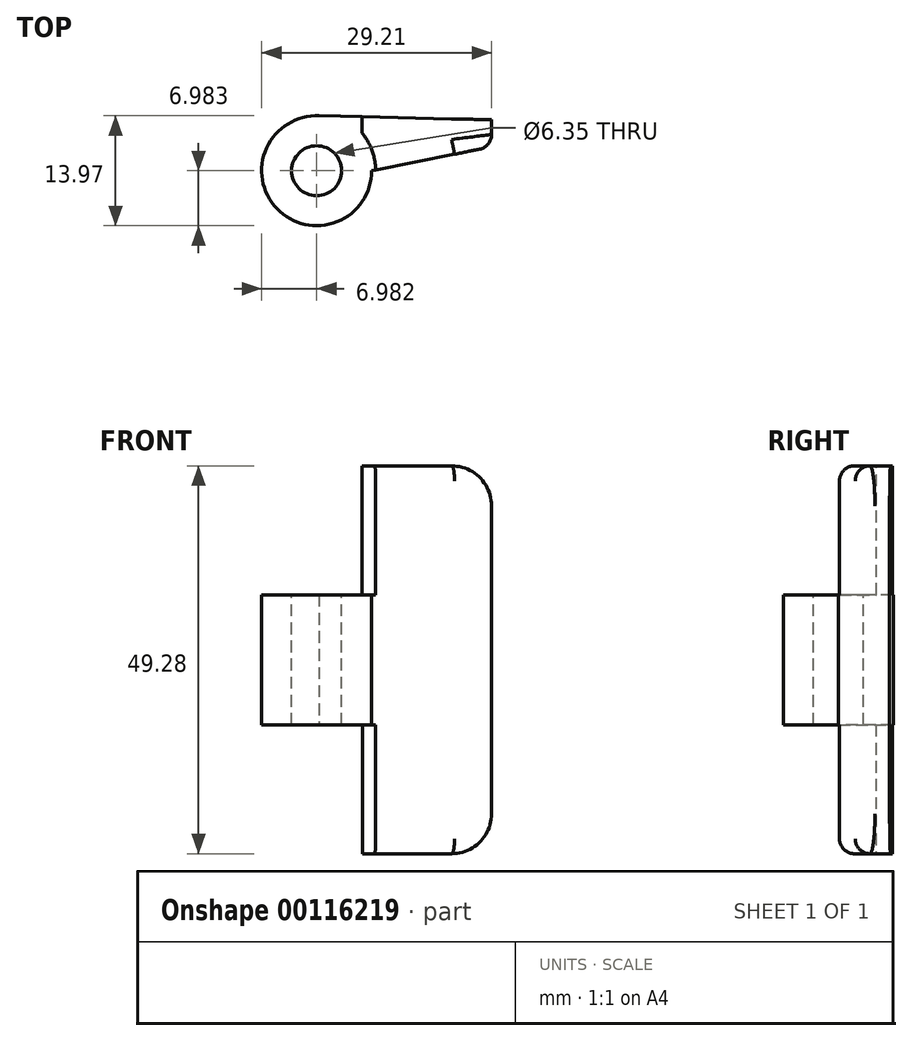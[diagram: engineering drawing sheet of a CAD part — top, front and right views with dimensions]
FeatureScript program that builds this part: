
annotation { "Feature Type Name" : "Feature", "Feature Type Description" : "" }
export const myFeature = defineFeature(function(context is Context, id is Id, definition is map)
    precondition{}
    {
        {
            var Q0;
            Q0=qCreatedBy(makeId("Top.planeOp"),FACE);
            var sketch = newSketch(context, id + "F0", { "sketchPlane" : qUnion([Q0])});
            skCircle(sketch, "E0", {"center": v(-0.5, -6.48) * mm, "radius": 6.99 * mm});
            skLineSegment(sketch, "E1", {"start": v(21.72, 0) * mm, "end": v(21.72, -3.43) * mm});
            skLineSegment(sketch, "E2", {"start": v(21.72, -3.43) * mm, "end": v(6.48, -6.48) * mm});
            skLineSegment(sketch, "E3", {"start": v(-0.5, 0.5) * mm, "end": v(21.72, 0) * mm});
            skSolve(sketch);
        }
        {
            var Q0;
            Q0 = qSketchRegion(id + "F0", true);
            extrude(context, id + "F1", {"entities" : qUnion([Q0]), "depth" : 49.28 * mm});
        }
        {
            var Q0;
            Q0=makeQuery(id+"F1.opExtrude","CAP_FACE",FACE,{"disambiguationData":[OSD([sQuery(id+"F0.wireOp",EDGE,"E0"),sQuery(id+"F0.wireOp",EDGE,"uuPIQ66o-S2XX-spIA-1Vip-rUJMBDG7AEti"),sQuery(id+"F0.wireOp",EDGE,"E1"),sQuery(id+"F0.wireOp",EDGE,"E2")])],"isStart":true});
            var sketch = newSketch(context, id + "F2", { "sketchPlane" : qUnion([Q0])});
            skCircle(sketch, "E4", {"center": v(-0.5, 6.48) * mm, "radius": 7.5 * mm});
            skSolve(sketch);
        }
        {
            var Q0;
            Q0 = qSketchRegion(id + "F2", true);
            extrude(context, id + "F3", {"entities" : qUnion([Q0]), "operationType" : NewBodyOperationType.REMOVE, "oppositeDirection" : true, "depth" : 16.38 * mm});
        }
        {
            var Q0;
            Q0=makeQuery(id+"F1.opExtrude","CAP_FACE",FACE,{"disambiguationData":[OSD([sQuery(id+"F0.wireOp",EDGE,"E0"),sQuery(id+"F0.wireOp",EDGE,"uuPIQ66o-S2XX-spIA-1Vip-rUJMBDG7AEti"),sQuery(id+"F0.wireOp",EDGE,"E1"),sQuery(id+"F0.wireOp",EDGE,"E2")])],"isStart":false});
            var sketch = newSketch(context, id + "F4", { "sketchPlane" : qUnion([Q0])});
            skCircle(sketch, "E5", {"center": v(-0.5, -6.48) * mm, "radius": 7.5 * mm});
            skSolve(sketch);
        }
        {
            var Q0;
            Q0 = qSketchRegion(id + "F4", true);
            extrude(context, id + "F5", {"entities" : qUnion([Q0]), "operationType" : NewBodyOperationType.REMOVE, "oppositeDirection" : true, "depth" : 16.38 * mm});
        }
        {
            var Q0;
            Q0=makeQuery(id+"F1.opExtrude","CAP_EDGE",EDGE,{"disambiguationData":[OSD([sQuery(id+"F0.wireOp",EDGE,"E1")])],"isStart":false});
            var Q1;
            Q1=makeQuery(id+"F1.opExtrude","CAP_EDGE",EDGE,{"disambiguationData":[OSD([sQuery(id+"F0.wireOp",EDGE,"E1")])],"isStart":true});
            fillet(context, id + "F6", {"entities" : qUnion([Q0, Q1]), "radius" : 5.08 * mm, "tangentPropagation" : true, "allowEdgeOverflow" : false});
        }
        {
            var Q0;
            Q0=makeQuery(id+"F1.opExtrude","CAP_EDGE",EDGE,{"disambiguationData":[OSD([sQuery(id+"F0.wireOp",EDGE,"E2")])],"isStart":false});
            fillet(context, id + "F7", {"entities" : qUnion([Q0]), "radius" : 1.9 * mm, "tangentPropagation" : true, "allowEdgeOverflow" : false});
        }
        {
            var Q0;
            Q0=makeQuery(id+"F5.boolean.opBoolean","COPY",FACE,{"derivedFrom":makeQuery(id+"F5.opExtrude","CAP_FACE",FACE,{"disambiguationData":[OSD([sQuery(id+"F4.wireOp",EDGE,"E5")])],"isStart":false})});
            var sketch = newSketch(context, id + "F8", { "sketchPlane" : qUnion([Q0])});
            skCircle(sketch, "E6", {"center": v(-0.5, -6.48) * mm, "radius": 3.18 * mm});
            skSolve(sketch);
        }
        {
            var Q0;
            Q0 = qSketchRegion(id + "F8", true);
            extrude(context, id + "F9", {"entities" : qUnion([Q0]), "operationType" : NewBodyOperationType.REMOVE, "endBound" : BoundingType.THROUGH_ALL, "oppositeDirection" : true, "depth" : 25.4 * mm});
        }
        {
            var Q0;
            Q0=makeQuery(id+"F1.opExtrude","CAP_FACE",FACE,{"disambiguationData":[OSD([sQuery(id+"F0.wireOp",EDGE,"E0"),sQuery(id+"F0.wireOp",EDGE,"E1"),sQuery(id+"F0.wireOp",EDGE,"E2"),sQuery(id+"F0.wireOp",EDGE,"E3")])],"isStart":false});
            var sketch = newSketch(context, id + "F10", { "sketchPlane" : qUnion([Q0])});
            skLineSegment(sketch, "E7.bottom", {"start": v(-0.7, 1.76) * mm, "end": v(5.25, 1.76) * mm});
            skLineSegment(sketch, "E7.top", {"start": v(-0.7, -2.99) * mm, "end": v(5.25, -2.99) * mm});
            skLineSegment(sketch, "E7.left", {"start": v(-0.7, 1.76) * mm, "end": v(-0.7, -2.99) * mm});
            skLineSegment(sketch, "E7.right", {"start": v(5.25, 1.76) * mm, "end": v(5.25, -2.99) * mm});
            skSolve(sketch);
        }
        {
            var Q0;
            Q0 = qSketchRegion(id + "F10", true);
            extrude(context, id + "F11", {"entities" : qUnion([Q0]), "operationType" : NewBodyOperationType.REMOVE, "oppositeDirection" : true, "depth" : 16.38 * mm});
        }
        {
            var Q0;
            Q0=makeQuery(id+"F1.opExtrude","CAP_FACE",FACE,{"disambiguationData":[OSD([sQuery(id+"F0.wireOp",EDGE,"E0"),sQuery(id+"F0.wireOp",EDGE,"E1"),sQuery(id+"F0.wireOp",EDGE,"E2"),sQuery(id+"F0.wireOp",EDGE,"E3")])],"isStart":true});
            var sketch = newSketch(context, id + "F12", { "sketchPlane" : qUnion([Q0])});
            skLineSegment(sketch, "E8.bottom", {"start": v(-0.7, -1.8) * mm, "end": v(5.31, -1.8) * mm});
            skLineSegment(sketch, "E8.top", {"start": v(-0.7, 3.08) * mm, "end": v(5.31, 3.08) * mm});
            skLineSegment(sketch, "E8.left", {"start": v(-0.7, -1.8) * mm, "end": v(-0.7, 3.08) * mm});
            skLineSegment(sketch, "E8.right", {"start": v(5.31, -1.8) * mm, "end": v(5.31, 3.08) * mm});
            skSolve(sketch);
        }
        {
            var Q0;
            Q0 = qSketchRegion(id + "F12", true);
            extrude(context, id + "F13", {"entities" : qUnion([Q0]), "operationType" : NewBodyOperationType.REMOVE, "oppositeDirection" : true, "depth" : 16.38 * mm});
        }
    });
